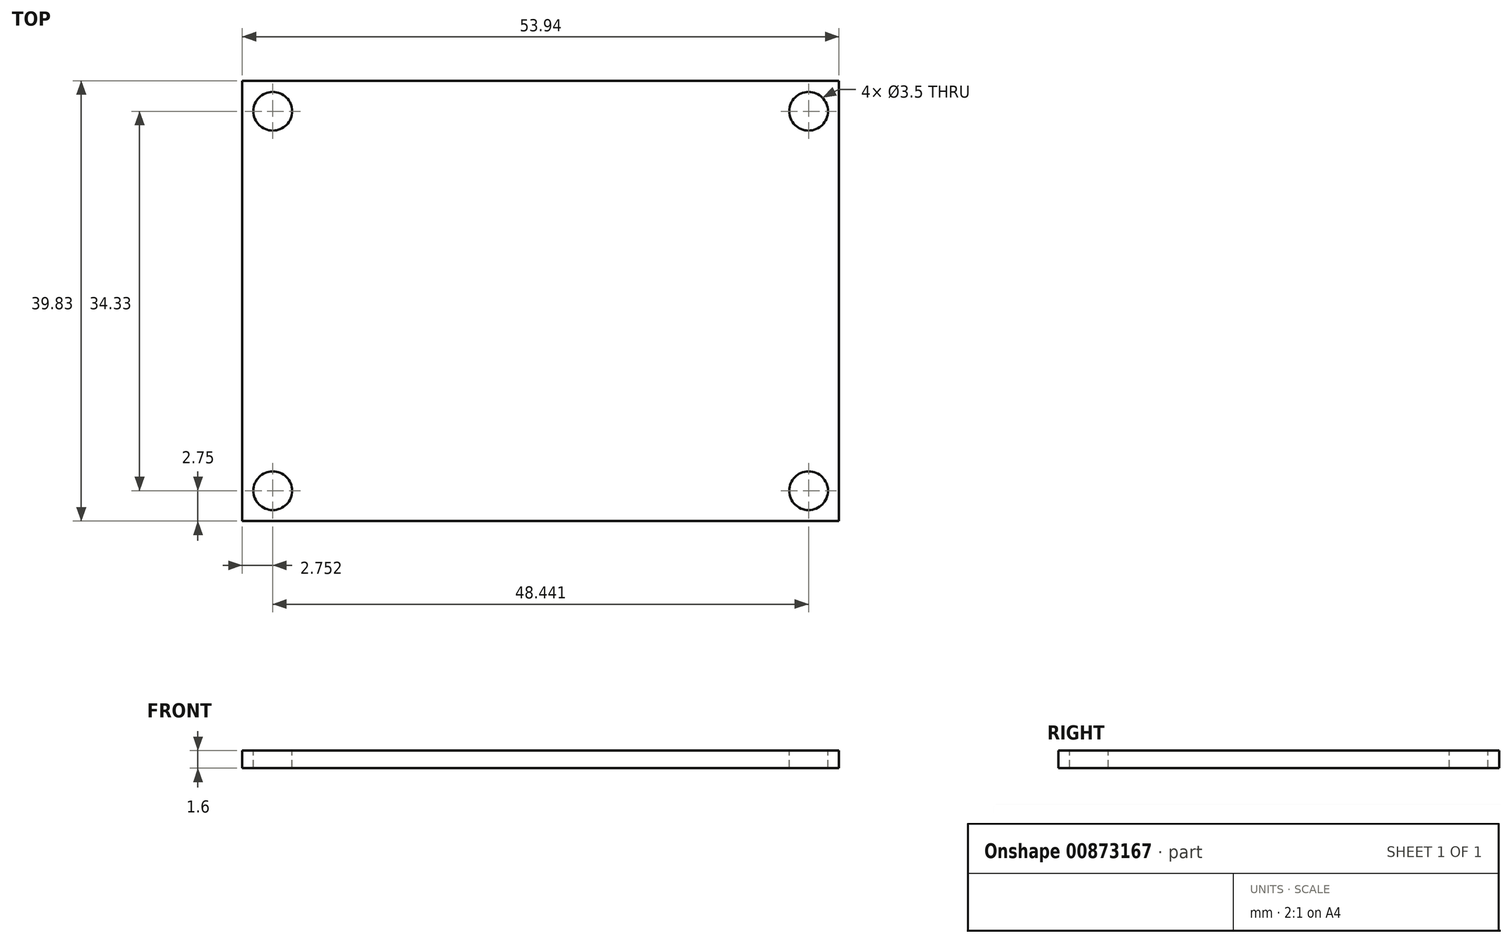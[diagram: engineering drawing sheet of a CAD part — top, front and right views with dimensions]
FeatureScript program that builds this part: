
annotation { "Feature Type Name" : "Feature", "Feature Type Description" : "" }
export const myFeature = defineFeature(function(context is Context, id is Id, definition is map)
    precondition{}
    {
        {
            var Q0;
            Q0=qCreatedBy(makeId("Top.planeOp"),FACE);
            var sketch = newSketch(context, id + "F0", { "sketchPlane" : qUnion([Q0])});
            skLineSegment(sketch, "E0.bottom", {"start": v(-10.94, 28.46) * mm, "end": v(43, 28.46) * mm});
            skLineSegment(sketch, "E0.top", {"start": v(-10.94, -11.37) * mm, "end": v(43, -11.37) * mm});
            skLineSegment(sketch, "E0.left", {"start": v(-10.94, 28.46) * mm, "end": v(-10.94, -11.37) * mm});
            skLineSegment(sketch, "E0.right", {"start": v(43, 28.46) * mm, "end": v(43, -11.37) * mm});
            skSolve(sketch);
        }
        {
            var Q0;
            Q0 = qSketchRegion(id + "F0", true);
            extrude(context, id + "F1", {"entities" : qUnion([Q0]), "depth" : 1.6 * mm, "offsetDistance" : 25 * mm});
        }
        {
            var Q0;
            Q0=makeQuery(id+"F1.opExtrude","CAP_FACE",FACE,{"disambiguationData":[OSD([sQuery(id+"F0.wireOp",EDGE,"E0.bottom"),sQuery(id+"F0.wireOp",EDGE,"E0.top"),sQuery(id+"F0.wireOp",EDGE,"E0.left"),sQuery(id+"F0.wireOp",EDGE,"E0.right")])],"isStart":false});
            var sketch = newSketch(context, id + "F2", { "sketchPlane" : qUnion([Q0])});
            skCircle(sketch, "E1", {"center": v(-8.19, 25.7) * mm, "radius": 1.75 * mm});
            skCircle(sketch, "E2", {"center": v(-8.19, -8.62) * mm, "radius": 1.75 * mm});
            skCircle(sketch, "E3", {"center": v(40.25, 25.7) * mm, "radius": 1.75 * mm});
            skCircle(sketch, "E4", {"center": v(40.25, -8.62) * mm, "radius": 1.75 * mm});
            skSolve(sketch);
        }
        {
            var Q0;
            Q0=sQuery(id+"F2.wireOp",VERTEX,"E1.center");
            var Q1;
            Q1=sQuery(id+"F2.wireOp",VERTEX,"E2.center");
            var Q2;
            Q2=sQuery(id+"F2.wireOp",VERTEX,"E4.center");
            var Q3;
            Q3=sQuery(id+"F2.wireOp",VERTEX,"E3.center");
            var Q4;
            Q4=makeQuery(id+"F1.opExtrude","SWEPT_BODY",BODY,{"disambiguationData":[OSD([sQuery(id+"F0.wireOp",EDGE,"E0.bottom"),sQuery(id+"F0.wireOp",EDGE,"E0.top"),sQuery(id+"F0.wireOp",EDGE,"E0.left"),sQuery(id+"F0.wireOp",EDGE,"E0.right")])]});
            hole(context, id + "F3", {"style" : HoleStyle.SIMPLE, "endStyle" : HoleEndStyle.THROUGH, "holeDiameter" : 3.5 * mm, "majorDiameter" : 5 * mm, "isTappedThrough" : true, "tappedDepth" : 12 * mm, "tapClearance" : 3, "locations" : qUnion([Q0, Q1, Q2, Q3]), "scope" : qUnion([Q4])});
        }
    });
